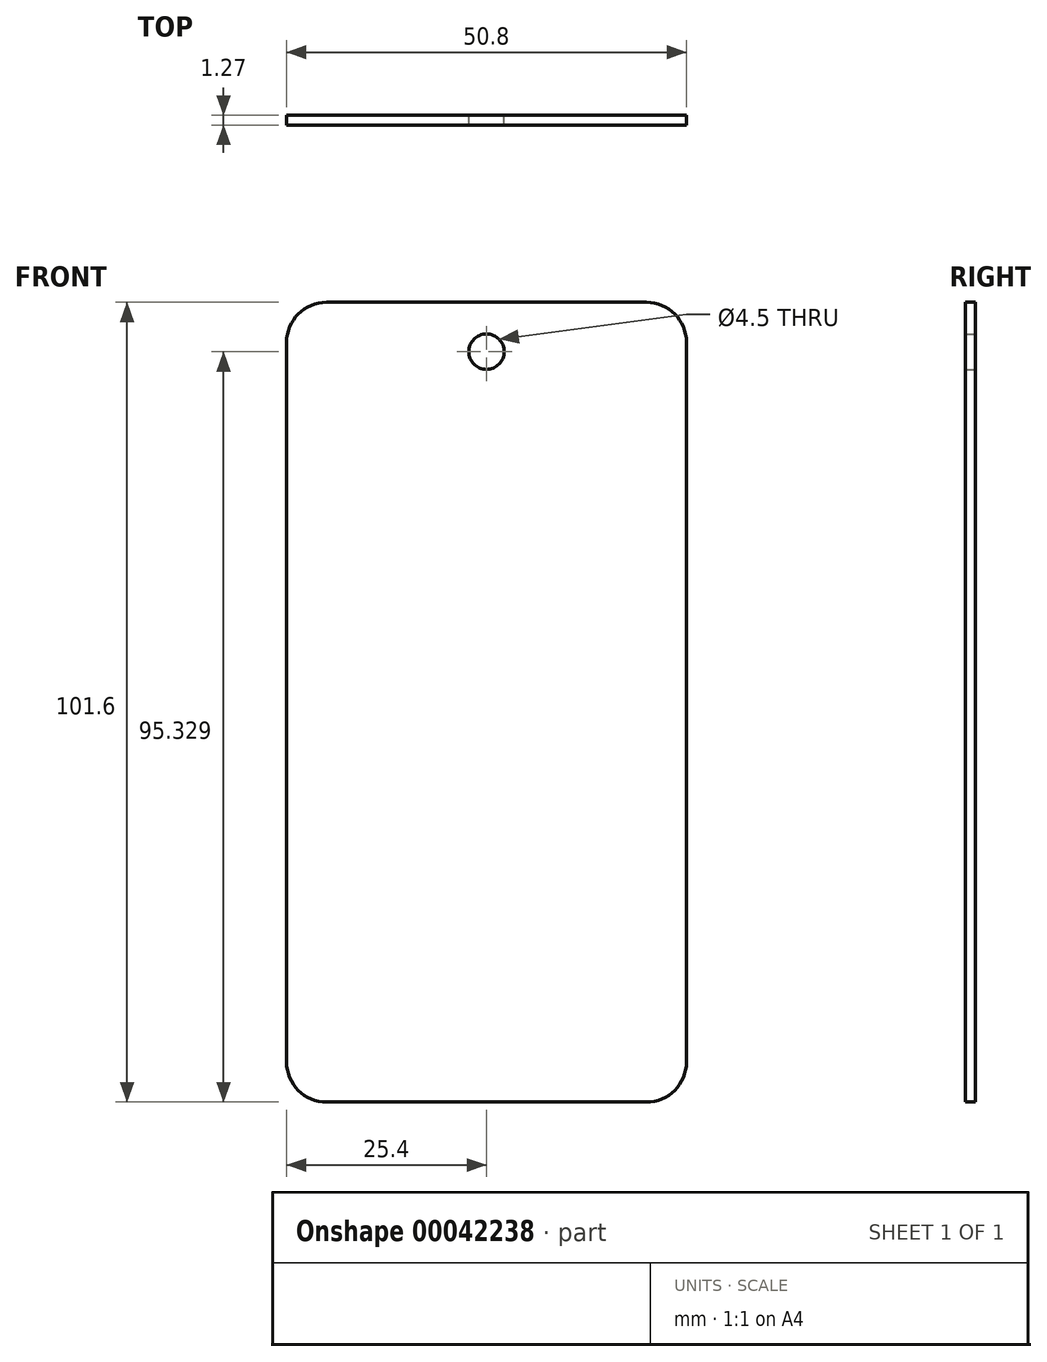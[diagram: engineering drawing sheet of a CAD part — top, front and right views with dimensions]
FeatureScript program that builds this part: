
annotation { "Feature Type Name" : "Feature", "Feature Type Description" : "" }
export const myFeature = defineFeature(function(context is Context, id is Id, definition is map)
    precondition{}
    {
        {
            var Q0;
            Q0=qCreatedBy(makeId("Front.planeOp"),FACE);
            var sketch = newSketch(context, id + "F0", { "sketchPlane" : qUnion([Q0])});
            skLineSegment(sketch, "E0", {"start": v(0, 0) * mm, "end": v(0, -50.8) * mm});
            skLineSegment(sketch, "E1", {"start": v(0, -50.8) * mm, "end": v(-50.8, -50.8) * mm});
            skLineSegment(sketch, "E2", {"start": v(-50.8, -50.8) * mm, "end": v(-50.8, 0) * mm});
            skLineSegment(sketch, "E3", {"start": v(-50.8, 0) * mm, "end": v(-50.8, 50.8) * mm});
            skLineSegment(sketch, "E4", {"start": v(0, 0) * mm, "end": v(0, 50.8) * mm});
            skLineSegment(sketch, "E5", {"start": v(-50.8, 50.8) * mm, "end": v(0, 50.8) * mm});
            skCircle(sketch, "E6", {"center": v(-25.4, 44.53) * mm, "radius": 2.25 * mm});
            skPoint(sketch, "E6.centerSnap0", {"position": v(-25.4, 50.8) * mm});
            skSolve(sketch);
        }
        {
            var Q0;
            Q0=makeQuery(id+"F0.imprint","IMPRINT",FACE,{"disambiguationData":[TD([[makeQuery(id+"F0.imprint","IMPRINT",EDGE,{"derivedFrom":sQuery(id+"F0.wireOp",EDGE,"E0")}),-1.0]])]});
            extrude(context, id + "F1", {"entities" : qUnion([Q0]), "depth" : 1.27 * mm});
        }
        {
            var Q0;
            Q0=makeQuery(id+"F1.opExtrude","SWEPT_EDGE",EDGE,{"disambiguationData":[OSD([sQuery(id+"F0.wireOp",EDGE,"E4"),sQuery(id+"F0.wireOp",EDGE,"E5")])]});
            var Q1;
            Q1=makeQuery(id+"F1.opExtrude","SWEPT_EDGE",EDGE,{"disambiguationData":[OSD([sQuery(id+"F0.wireOp",EDGE,"E3"),sQuery(id+"F0.wireOp",EDGE,"E5")])]});
            var Q2;
            Q2=makeQuery(id+"F1.opExtrude","SWEPT_EDGE",EDGE,{"disambiguationData":[OSD([sQuery(id+"F0.wireOp",EDGE,"E1"),sQuery(id+"F0.wireOp",EDGE,"E2")])]});
            var Q3;
            Q3=makeQuery(id+"F1.opExtrude","SWEPT_EDGE",EDGE,{"disambiguationData":[OSD([sQuery(id+"F0.wireOp",EDGE,"E0"),sQuery(id+"F0.wireOp",EDGE,"E1")])]});
            fillet(context, id + "F2", {"entities" : qUnion([Q0, Q1, Q2, Q3]), "radius" : 5.08 * mm, "tangentPropagation" : true, "allowEdgeOverflow" : false});
        }
    });
